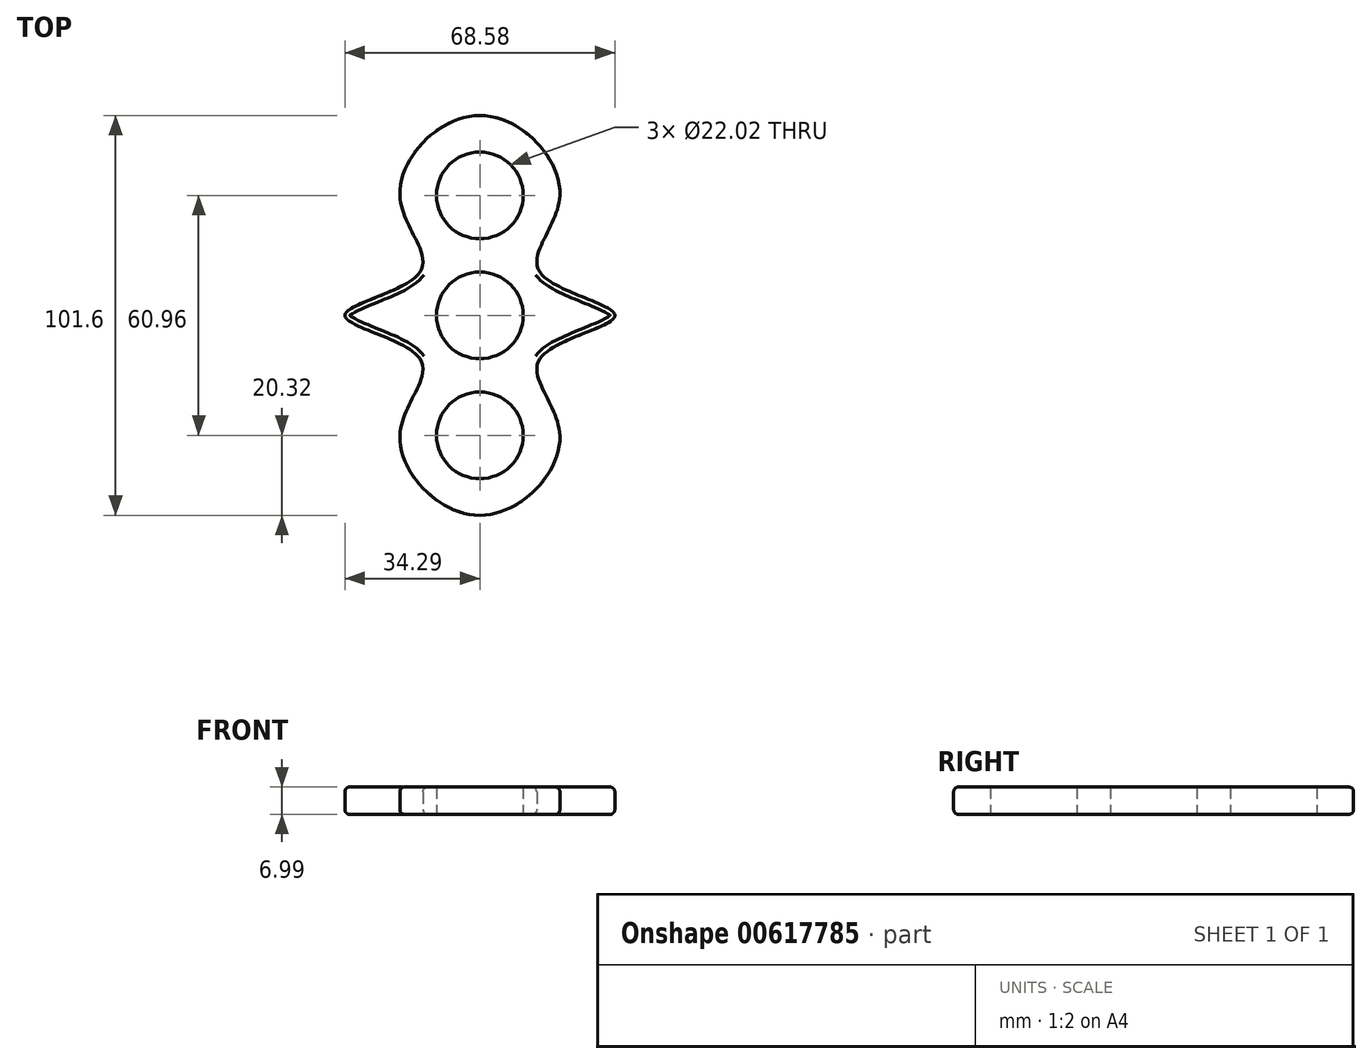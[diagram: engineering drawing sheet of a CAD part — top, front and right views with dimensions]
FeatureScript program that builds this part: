
annotation { "Feature Type Name" : "Feature", "Feature Type Description" : "" }
export const myFeature = defineFeature(function(context is Context, id is Id, definition is map)
    precondition{}
    {
        {
            var Q0;
            Q0=qCreatedBy(makeId("Top.planeOp"),FACE);
            var sketch = newSketch(context, id + "F0", { "sketchPlane" : qUnion([Q0])});
            skCircle(sketch, "E0", {"center": v(0, 0) * mm, "radius": 11.01 * mm});
            skCircle(sketch, "E1", {"center": v(0, 30.48) * mm, "radius": 11.01 * mm});
            skCircle(sketch, "E2", {"center": v(0, -30.48) * mm, "radius": 11.01 * mm});
            skLineSegment(sketch, "E3", {"start": v(0, 0) * mm, "end": v(0, -30.48) * mm});
            skLineSegment(sketch, "E4", {"start": v(0, 0) * mm, "end": v(0, 30.48) * mm});
            skFitSpline(sketch, "E5", {"points": [v(-15.24, -11.01) * mm, v(-34.3, 0) * mm, v(-15.24, 11.01) * mm, v(-20.32, 30.48) * mm, v(0, 50.8) * mm, v(20.32, 30.48) * mm, v(15.24, 11.01) * mm, v(34.3, 0) * mm, v(15.24, -11.01) * mm, v(20.32, -30.48) * mm, v(0, -50.8) * mm, v(-20.32, -30.48) * mm, v(-15.24, -11.01) * mm]});
            skLineSegment(sketch, "E6", {"start": v(0, 30.48) * mm, "end": v(0, 50.8) * mm});
            skLineSegment(sketch, "E7", {"start": v(0, -30.48) * mm, "end": v(0, -50.8) * mm});
            skLineSegment(sketch, "E8", {"start": v(0, -30.48) * mm, "end": v(-20.32, -30.48) * mm});
            skLineSegment(sketch, "E9", {"start": v(0, -30.48) * mm, "end": v(20.32, -30.48) * mm});
            skLineSegment(sketch, "E10", {"start": v(0, 30.48) * mm, "end": v(20.32, 30.48) * mm});
            skLineSegment(sketch, "E11", {"start": v(0, 30.48) * mm, "end": v(-20.32, 30.48) * mm});
            skLineSegment(sketch, "E12", {"start": v(0, 0) * mm, "end": v(34.3, 0) * mm});
            skLineSegment(sketch, "E13", {"start": v(0, 0) * mm, "end": v(-34.3, 0) * mm});
            skLineSegment(sketch, "E14", {"start": v(-15.24, -11.01) * mm, "end": v(15.24, -11.01) * mm});
            skLineSegment(sketch, "E15", {"start": v(-15.24, 11.01) * mm, "end": v(15.24, 11.01) * mm});
            skPoint(sketch, "E16", {"position": v(0, 11.01) * mm});
            skPoint(sketch, "E17", {"position": v(0, -11.01) * mm});
            skPoint(sketch, "E18", {"position": v(0, -15.24) * mm});
            skSolve(sketch);
        }
        {
            var Q0;
            Q0 = qSketchRegion(id + "F0", true);
            extrude(context, id + "F1", {"entities" : qUnion([Q0]), "depth" : 7 * mm, "offsetDistance" : 25.4 * mm});
        }
        {
            var Q0;
            Q0=makeQuery(id+"F1.opExtrude","CAP_EDGE",EDGE,{"disambiguationData":[OSD([sQuery(id+"F0.wireOp",EDGE,"E5")])],"isStart":true});
            var Q1;
            Q1=makeQuery(id+"F1.opExtrude","CAP_EDGE",EDGE,{"disambiguationData":[OSD([sQuery(id+"F0.wireOp",EDGE,"E5")])],"isStart":false});
            fillet(context, id + "F2", {"entities" : qUnion([Q0, Q1]), "radius" : 1.27 * mm, "tangentPropagation" : true, "allowEdgeOverflow" : false});
        }
    });
